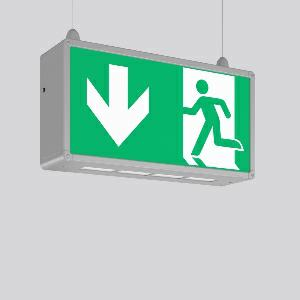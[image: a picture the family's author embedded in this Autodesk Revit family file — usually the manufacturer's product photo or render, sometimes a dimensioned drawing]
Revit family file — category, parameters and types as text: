
# Revit family: rechteck_seilpendel_671367_004_89_dec6
name_source: partatom
category: Lighting Fixtures
units: mm (PartAtom-declared; Revit-internal decimal feet)

## family parameters
Cut with Voids When Loaded = No
Host = Face
Light Source = No
Part Type = Normal
Room Calculation Point = No
Round Connector Dimension = Use Diameter
Shared = No

## types (1)
- RECHTECK seilpendel
    Apparent Load = 0 VA
    Default Elevation = 1800 mm
    Description = Series: RECHTECK
Rectangular pendant luminaire in classic design. For escape route identification. Housing: aluminium, with plastic corner connectors. Display panels: plastic, opal, with motifs on one side/on both sides. Pendant luminaires (suspension provided on site) ready for connection to two suspension cables or chains. Driver integrated. Suitable for connection to central battery systems. With AC Control monitoring module for LUXIFAIR central battery units. Please indicate legend number when placing your order! 
Colour: anodised aluminium
Length: 485 mm
Width: 125 mm
Height: 250 mm
Weight: 2.67 kg
Operating mode: maintained power mode
Viewing Distance: 43 m
Lamp: LED
Socket: without socket
Colour temperature: 6500K
Colour rendering index (CRI): 70
System power: 9.1 W
Control gear: Regulated power supply
Protection class: I
Type of protection: IP 44
    Height = 250 mm
    Lamp = 0 x
    Length = 485 mm
    Luminous efficacy = 0 lm/W
    Manufacturer = RZB
    ModVariant = No
    Model = 671367.004.89
    Mounting Place = Ceiling
    Mounting Type = Pendant
    Number of Poles = 1
    OnlyDefault = Yes
    Power Factor = 1
    Product Name = RECHTECK seilpendel
    Product group = Pendant luminaires
    ProductGroupID = 902
    Protection Class = Protection class I
    Protection Degree = IP 44
    RLX_Detail_Level = 1
    RLX_Emergency_Light_Flux = 0 lm
    RLX_Emergency_Type = 0
    RLX_Emergency_Type_DB = No
    RlxData = <blob elided: 57693 chars, md5=a8503577>
    Standby Power = 0 W
    System Light Flux = 0 lm
    System Power = 0 W
    Type Comments = Product without accessories
    Type Image = 671351.004.jpg
    URL = http://relux.com
    VarID = ---
    Voltage = 230 V
    Voltage Range = 220-240 V
    Weight = 0.00 kg
    Width = 125 mm

## geometry (parser evidence)
native form markers: Blend x4, Sweep x11
no freeform markers — native parametric forms only
